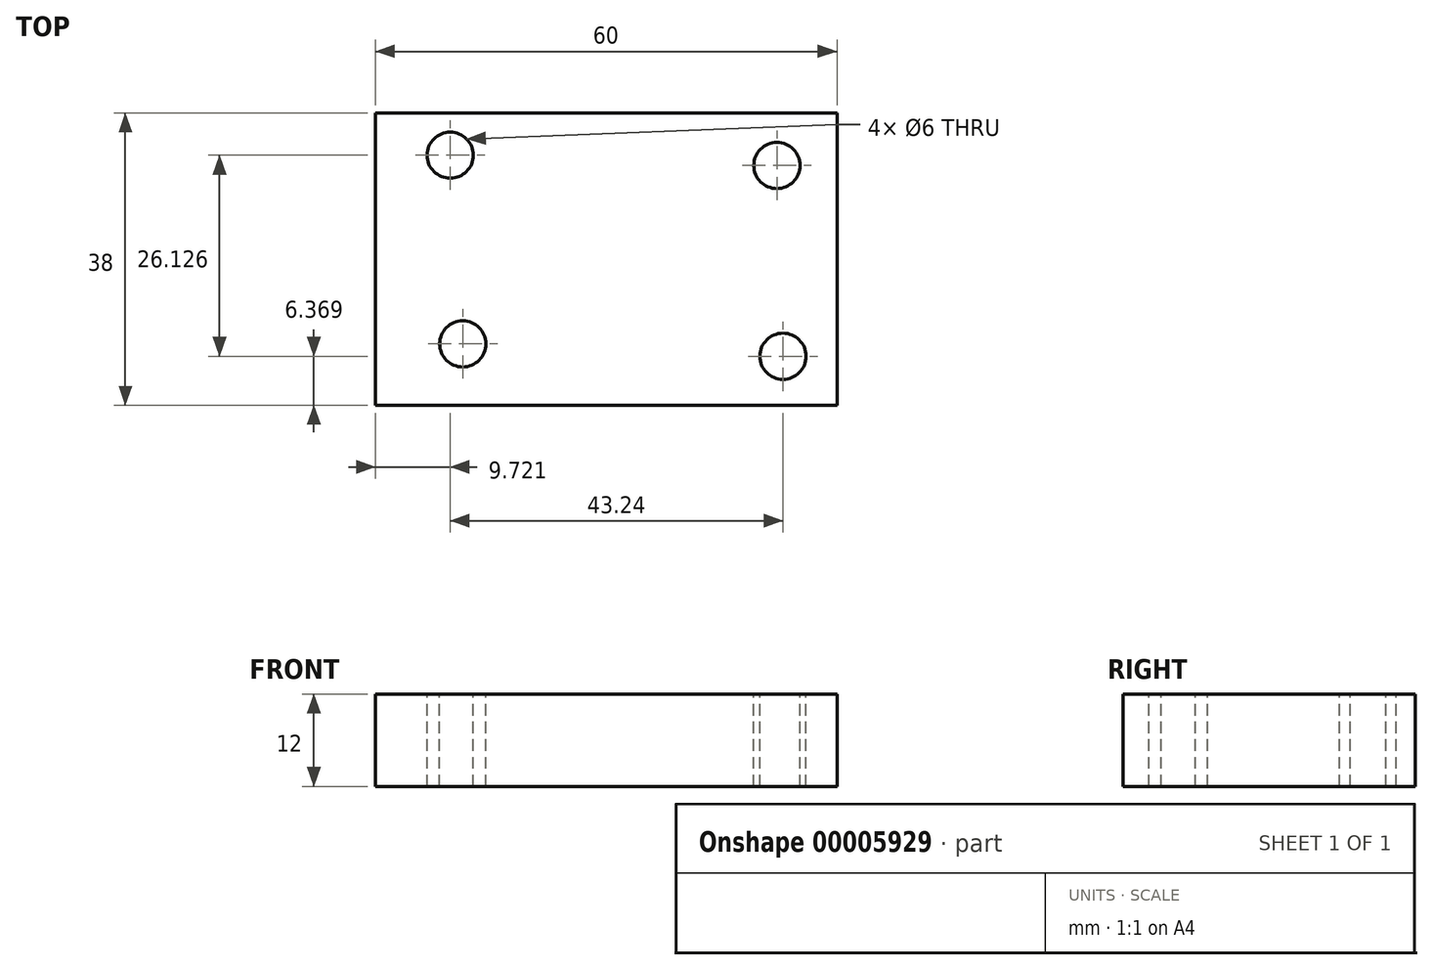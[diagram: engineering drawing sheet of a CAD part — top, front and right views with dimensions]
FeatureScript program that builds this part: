
annotation { "Feature Type Name" : "Feature", "Feature Type Description" : "" }
export const myFeature = defineFeature(function(context is Context, id is Id, definition is map)
    precondition{}
    {
        {
            var Q0;
            Q0=qCreatedBy(makeId("Top.planeOp"),FACE);
            var sketch = newSketch(context, id + "F0", { "sketchPlane" : qUnion([Q0])});
            skLineSegment(sketch, "E0.bottom", {"start": v(33.72, 23.04) * mm, "end": v(-26.28, 23.04) * mm});
            skLineSegment(sketch, "E0.top", {"start": v(33.72, -14.96) * mm, "end": v(-26.28, -14.96) * mm});
            skLineSegment(sketch, "E0.left", {"start": v(33.72, 23.04) * mm, "end": v(33.72, -14.96) * mm});
            skLineSegment(sketch, "E0.right", {"start": v(-26.28, 23.04) * mm, "end": v(-26.28, -14.96) * mm});
            skSolve(sketch);
        }
        {
            var Q0;
            Q0=makeQuery(id+"F0.imprint","IMPRINT",FACE,{"disambiguationData":[TD([[makeQuery(id+"F0.imprint","IMPRINT",EDGE,{"derivedFrom":sQuery(id+"F0.wireOp",EDGE,"E0.bottom")}),1.0]])]});
            extrude(context, id + "F1", {"entities" : qUnion([Q0]), "depth" : 12 * mm});
        }
        {
            var Q0;
            Q0=makeQuery(id+"F1.opExtrude","CAP_FACE",FACE,{"disambiguationData":[OSD([sQuery(id+"F0.wireOp",EDGE,"E0.bottom"),sQuery(id+"F0.wireOp",EDGE,"E0.top"),sQuery(id+"F0.wireOp",EDGE,"E0.left"),sQuery(id+"F0.wireOp",EDGE,"E0.right")])],"isStart":false});
            var sketch = newSketch(context, id + "F2", { "sketchPlane" : qUnion([Q0])});
            skCircle(sketch, "E1", {"center": v(-16.56, 17.54) * mm, "radius": 3 * mm});
            skSolve(sketch);
        }
        {
            var Q0;
            Q0=makeQuery(id+"F2.imprint","IMPRINT",FACE,{"disambiguationData":[TD([[makeQuery(id+"F2.imprint","IMPRINT",EDGE,{"derivedFrom":sQuery(id+"F2.wireOp",EDGE,"E1")}),-1.0]])]});
            var sketch = newSketch(context, id + "F3", { "sketchPlane" : qUnion([Q0])});
            skCircle(sketch, "E2", {"center": v(25.9, 16.2) * mm, "radius": 3 * mm});
            skSolve(sketch);
        }
        {
            var Q0;
            Q0=makeQuery(id+"F2.imprint","IMPRINT",FACE,{"disambiguationData":[TD([[makeQuery(id+"F2.imprint","IMPRINT",EDGE,{"derivedFrom":sQuery(id+"F2.wireOp",EDGE,"E1")}),-1.0]])]});
            var sketch = newSketch(context, id + "F4", { "sketchPlane" : qUnion([Q0])});
            skCircle(sketch, "E3", {"center": v(26.68, -8.6) * mm, "radius": 3 * mm});
            skSolve(sketch);
        }
        {
            var Q0;
            Q0=makeQuery(id+"F2.imprint","IMPRINT",FACE,{"disambiguationData":[TD([[makeQuery(id+"F2.imprint","IMPRINT",EDGE,{"derivedFrom":sQuery(id+"F2.wireOp",EDGE,"E1")}),-1.0]])]});
            var sketch = newSketch(context, id + "F5", { "sketchPlane" : qUnion([Q0])});
            skCircle(sketch, "E4", {"center": v(-14.93, -6.98) * mm, "radius": 3 * mm});
            skSolve(sketch);
        }
        {
            var Q0;
            Q0=qSketchRegion(id+"F4",true);
            extrude(context, id + "F6", {"entities" : qUnion([Q0]), "operationType" : NewBodyOperationType.REMOVE, "oppositeDirection" : true, "depth" : 25 * mm});
        }
        {
            var Q0;
            Q0=qSketchRegion(id+"F3",true);
            extrude(context, id + "F7", {"entities" : qUnion([Q0]), "operationType" : NewBodyOperationType.REMOVE, "oppositeDirection" : true, "depth" : 25 * mm});
        }
        {
            var Q0;
            Q0=qSketchRegion(id+"F2",true);
            extrude(context, id + "F8", {"entities" : qUnion([Q0]), "operationType" : NewBodyOperationType.REMOVE, "oppositeDirection" : true, "depth" : 25 * mm});
        }
        {
            var Q0;
            Q0=makeQuery(id+"F5.imprint","IMPRINT",FACE,{"disambiguationData":[TD([[makeQuery(id+"F5.imprint","IMPRINT",EDGE,{"derivedFrom":sQuery(id+"F5.wireOp",EDGE,"E4")}),1.0]])]});
            var Q1;
            Q1=sQuery(id+"F5.wireOp",EDGE,"E4");
            extrude(context, id + "F9", {"entities" : qUnion([Q0]), "operationType" : NewBodyOperationType.REMOVE, "surfaceEntities" : qUnion([Q1]), "oppositeDirection" : true, "depth" : 25 * mm});
        }
    });
